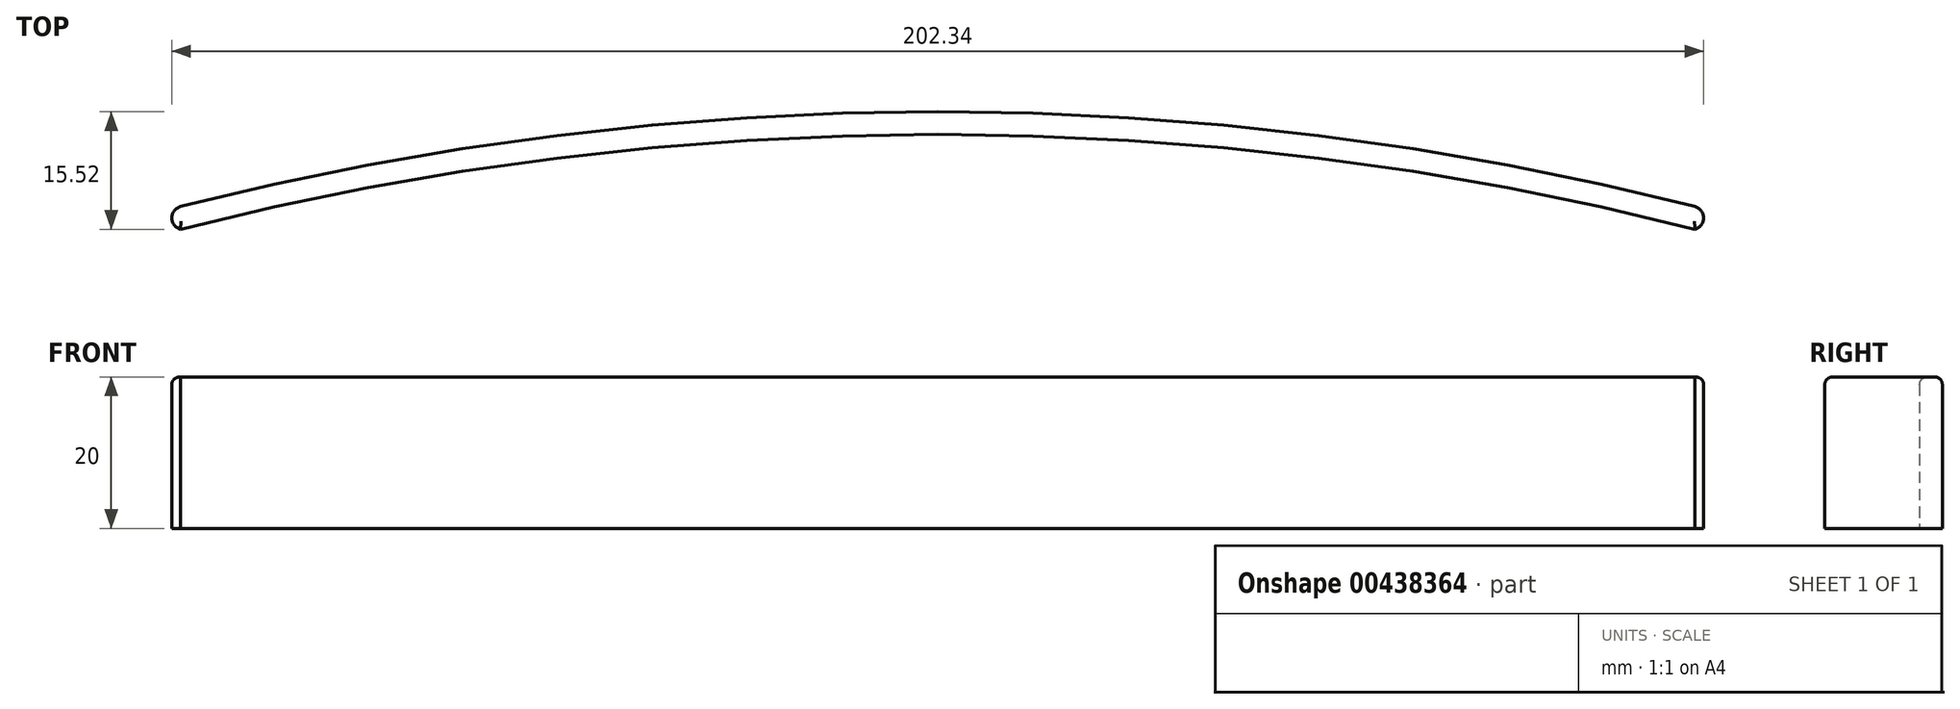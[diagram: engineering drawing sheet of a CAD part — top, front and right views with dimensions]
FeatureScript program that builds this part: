
annotation { "Feature Type Name" : "Feature", "Feature Type Description" : "" }
export const myFeature = defineFeature(function(context is Context, id is Id, definition is map)
    precondition{}
    {
        {
            var Q0;
            Q0=qCreatedBy(makeId("Top.planeOp"),FACE);
            var sketch = newSketch(context, id + "F0", { "sketchPlane" : qUnion([Q0])});
            skArc(sketch, "E0", {"start": v(100, -5.67) * mm, "mid": v(0, 6.85) * mm, "end": v(-100, -5.67) * mm});
            skArc(sketch, "E1", {"start": v(100, -2.67) * mm, "mid": v(0, 9.85) * mm, "end": v(-100, -2.67) * mm});
            skArc(sketch, "E2", {"start": v(-100, -2.67) * mm, "mid": v(-101.17, -4.17) * mm, "end": v(-100, -5.67) * mm});
            skArc(sketch, "E3", {"start": v(100, -2.67) * mm, "mid": v(101.17, -4.17) * mm, "end": v(100, -5.67) * mm});
            skSolve(sketch);
        }
        {
            var Q0;
            Q0=makeQuery(id+"F0.imprint","IMPRINT",FACE,{"disambiguationData":[TD([[makeQuery(id+"F0.imprint","IMPRINT",EDGE,{"derivedFrom":sQuery(id+"F0.wireOp",EDGE,"E0")}),-1.0]])]});
            extrude(context, id + "F1", {"entities" : qUnion([Q0]), "depth" : 20 * mm});
        }
        {
            var Q0;
            Q0=makeQuery(id+"F1.opExtrude","CAP_EDGE",EDGE,{"disambiguationData":[OSD([sQuery(id+"F0.wireOp",EDGE,"E0")])],"isStart":false});
            var Q1;
            Q1=makeQuery(id+"F1.opExtrude","CAP_EDGE",EDGE,{"disambiguationData":[OSD([sQuery(id+"F0.wireOp",EDGE,"E2")])],"isStart":false});
            fillet(context, id + "F2", {"entities" : qUnion([Q0, Q1]), "radius" : 1 * mm, "tangentPropagation" : true, "allowEdgeOverflow" : false});
        }
    });
